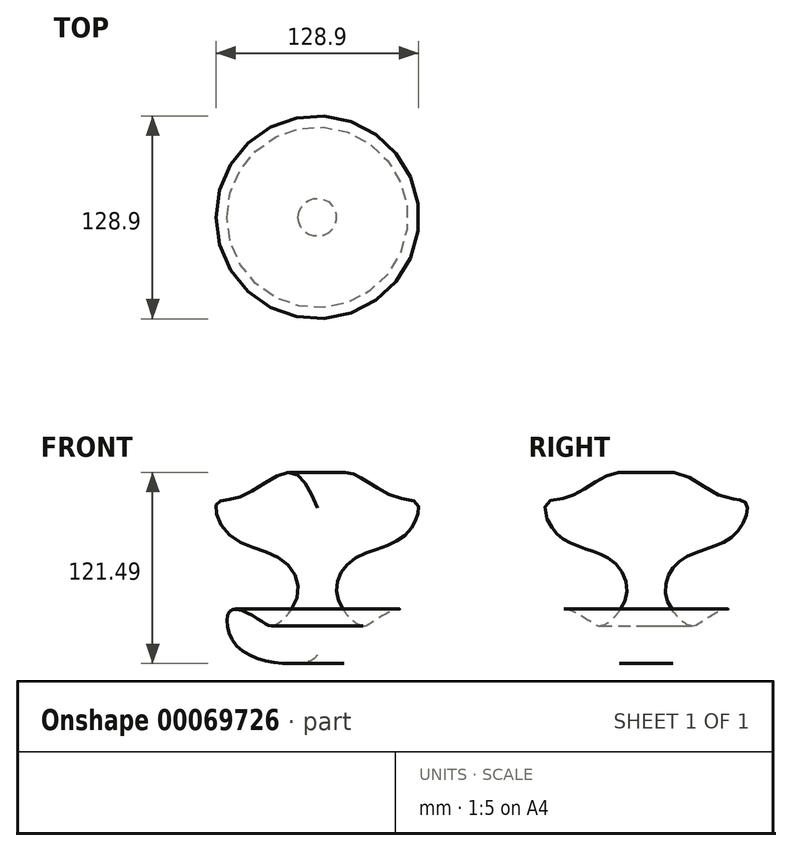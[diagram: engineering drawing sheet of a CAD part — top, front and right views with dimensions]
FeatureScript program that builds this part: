
annotation { "Feature Type Name" : "Feature", "Feature Type Description" : "" }
export const myFeature = defineFeature(function(context is Context, id is Id, definition is map)
    precondition{}
    {
        {
            var Q0;
            Q0=qCreatedBy(makeId("Front.planeOp"),FACE);
            var sketch = newSketch(context, id + "F0", { "sketchPlane" : qUnion([Q0])});
            skFitSpline(sketch, "E0", {"points": [v(0, -50.49) * mm, v(-6.28, -54.83) * mm, v(-50.24, -45.65) * mm, v(-54.6, -21.98) * mm, v(-35.27, -29.23) * mm, v(-27.05, -31.64) * mm, v(-12.56, -12.8) * mm, v(-23.19, 10.39) * mm, v(-55.56, 25.36) * mm, v(-63.77, 45.65) * mm, v(-48.8, 50) * mm, v(-16.9, 65.46) * mm, v(0, 42.76) * mm], "startDerivative": vector(-78.68, -103.25) * mm, "endDerivative": vector(148.73, -359.23) * mm});
            skLineSegment(sketch, "E1", {"start": v(0, 72.6) * mm, "end": v(0, -67.56) * mm, "construction": true});
            skLineSegment(sketch, "E2", {"start": v(0, 42.76) * mm, "end": v(0, -50.49) * mm});
            skSolve(sketch);
        }
        {
            var Q0;
            Q0=makeQuery(id+"F0.imprint","IMPRINT",FACE,{"disambiguationData":[TD([[makeQuery(id+"F0.imprint","IMPRINT",EDGE,{"derivedFrom":sQuery(id+"F0.wireOp",EDGE,"E0")}),-1.0]])]});
            var Q1;
            Q1=sQuery(id+"F0.wireOp",EDGE,"E1");
            revolve(context, id + "F1", {"entities" : qUnion([Q0]), "axis" : qUnion([Q1]), "revolveType" : RevolveType.FULL});
        }
    });
